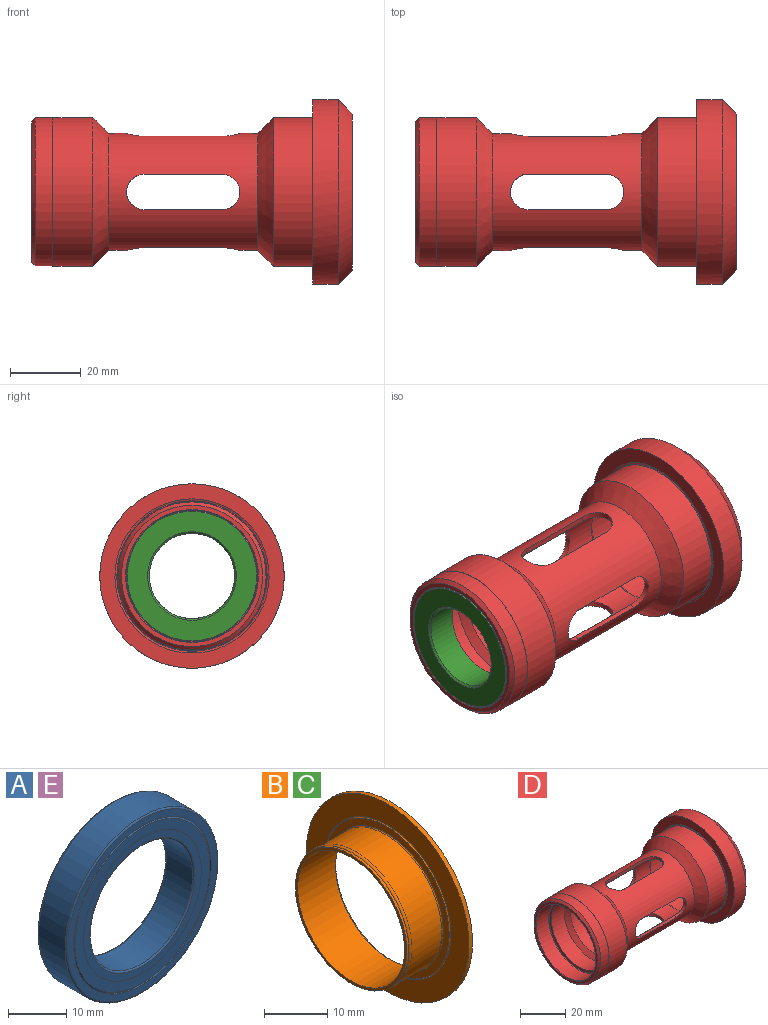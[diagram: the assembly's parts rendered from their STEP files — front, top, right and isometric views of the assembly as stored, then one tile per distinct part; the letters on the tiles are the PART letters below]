
ASSEMBLY  parts=5 mates=2
PART A: 38 faces, bbox 40x7x40 mm
  f0: torus R=15.5mm, axis (0,1,0), area 122.3mm2, adj f12,f37
  f1: cylinder r=12.5mm len=25mm, axis (0,1,0), area 502.7mm2, adj f2,f3
  f2: torus R=12.8mm, axis (0,1,0), area 37.3mm2, adj f1,f4
  f3: torus R=12.8mm, axis (0,1,0), area 37.3mm2, adj f1,f5
  f4: plane 28.62x28.62mm, normal (0,-1,0), area 128.4mm2, adj f2,f6
  f5: plane 28.62x28.62mm, normal (0,1,0), area 128.4mm2, adj f3,f8
  f6: cylinder r=14.31mm len=28.62mm, axis (0,1,0), area 62.9mm2, adj f4,f9
  f7: torus R=15.5mm, axis (0,1,0), area 122.3mm2, adj f10,f36
  f8: cylinder r=14.31mm len=28.62mm, axis (0,1,0), area 62.9mm2, adj f5,f11
  f9: plane 29.2x29.2mm, normal (0,-1,0), area 26.5mm2, adj f6,f10
  f10: cylinder r=14.6mm len=29.2mm, axis (0,1,0), area 113.9mm2, adj f7,f9
  f11: plane 29.2x29.2mm, normal (0,1,0), area 26.5mm2, adj f8,f12
  f12: cylinder r=14.6mm len=29.2mm, axis (0,1,0), area 113.9mm2, adj f0,f11
  f13: torus R=15.5mm, axis (0,1,0), area 146.2mm2, adj f35,f37
  f14: cylinder r=18.5mm len=37mm, axis (0,1,0), area 743.9mm2, adj f15,f16
  f15: torus R=18.2mm, axis (0,1,0), area 54.5mm2, adj f14,f17
  f16: torus R=18.2mm, axis (0,1,0), area 54.5mm2, adj f14,f18
  f17: plane 36.4x36.4mm, normal (0,-1,0), area 161.5mm2, adj f15,f19
  f18: plane 36.4x36.4mm, normal (0,1,0), area 161.5mm2, adj f16,f20
  f19: cylinder r=16.73mm len=33.46mm, axis (0,1,0), area 35.7mm2, adj f17,f21
  f20: cylinder r=16.73mm len=33.46mm, axis (0,1,0), area 35.7mm2, adj f18,f22
  f21: cone r=16.56mm half-angle=45deg, axis (0,1,0), area 50mm2, adj f19,f23
  f22: cone r=16.56mm half-angle=45deg, axis (0,-1,0), area 50mm2, adj f20,f24
  f23: plane 32.78x32.78mm, normal (0,-1,0), area 199.7mm2, adj f21,f25
  f24: plane 32.78x32.78mm, normal (0,1,0), area 199.7mm2, adj f22,f26
  f25: cylinder r=14.32mm len=28.64mm, axis (0,-1,0), area 62.1mm2, adj f23,f27
  f26: cylinder r=14.32mm len=28.64mm, axis (0,1,0), area 62.1mm2, adj f24,f28
  f27: plane 33.46x33.46mm, normal (0,1,0), area 235.1mm2, adj f25,f29
  f28: plane 33.46x33.46mm, normal (0,-1,0), area 235.1mm2, adj f26,f31
  f29: cylinder r=16.73mm len=33.46mm, axis (0,1,0), area 1.1mm2, adj f27,f32
  f30: torus R=15.5mm, axis (0,1,0), area 146.2mm2, adj f33,f36
  f31: cylinder r=16.73mm len=33.46mm, axis (0,1,0), area 1.1mm2, adj f28,f34
  f32: plane 33.46x33.46mm, normal (0,-1,0), area 34.1mm2, adj f29,f33
  f33: cylinder r=16.4mm len=32.8mm, axis (0,1,0), area 127.9mm2, adj f30,f32
  f34: plane 33.46x33.46mm, normal (0,1,0), area 34.1mm2, adj f31,f35
  f35: cylinder r=16.4mm len=32.8mm, axis (0,1,0), area 127.9mm2, adj f13,f34
  f36: plane 34.46x34.46mm, normal (0,-1,0), area 336.8mm2, adj f7,f30
  f37: plane 34.46x34.46mm, normal (0,1,0), area 336.8mm2, adj f0,f13
PART B: 12 faces, bbox 9x36.5x36.5 mm
  f0: cylinder r=12.5mm len=25mm, axis (-1,0,0), area 526.2mm2, adj f1,f11
  f1: torus R=12.25mm, axis (-1,0,0), area 56.7mm2, adj f0,f2
  f2: cylinder r=12.5mm len=25mm, axis (-1,0,0), area 37.3mm2, adj f1,f3
  f3: plane 25x25mm, normal (-1,0,0), area 38.5mm2, adj f2,f4
  f4: cylinder r=12mm len=24mm, axis (-1,0,0), area 640.9mm2, adj f3,f9
  f5: plane 36.5x36.5mm, normal (1,0,0), area 555.5mm2, adj f6,f9
  f6: cylinder r=18.25mm len=36.5mm, axis (-1,0,0), area 91.7mm2, adj f5,f7
  f7: plane 36.5x36.5mm, normal (-1,0,0), area 412.9mm2, adj f6,f10
  f8: plane 28x28mm, normal (-1,0,0), area 109mm2, adj f10,f11
  f9: cone r=12.5mm half-angle=45deg, axis (1,0,0), area 54.4mm2, adj f4,f5
  f10: torus R=14.2mm, axis (1,0,0), area 27.8mm2, adj f7,f8
  f11: torus R=12.7mm, axis (1,0,0), area 24.8mm2, adj f0,f8
PART C: same geometry as B
PART D: 44 faces, bbox 90.5x52x52 mm
  f0: plane 22x1.58mm, normal (0,-1,0), area 34.8mm2, adj f1,f3,f21,f31
  f1: cylinder r=5mm len=10mm, axis (0,0,1), area 24.2mm2, adj f0,f2,f21,f31
  f2: plane 22x1.58mm, normal (0,1,0), area 34.8mm2, adj f1,f3,f21,f31
  f3: cylinder r=5mm len=10mm, axis (0,0,1), area 24.2mm2, adj f0,f2,f21,f31
  f4: plane 22x1.58mm, normal (0,0,1), area 34.8mm2, adj f5,f7,f21,f31
  f5: cylinder r=5mm len=10mm, axis (0,1,0), area 24.2mm2, adj f4,f6,f21,f31
  f6: plane 22x1.58mm, normal (0,0,-1), area 34.8mm2, adj f5,f7,f21,f31
  f7: cylinder r=5mm len=10mm, axis (0,1,0), area 24.2mm2, adj f4,f6,f21,f31
  f8: plane 22x1.58mm, normal (0,1,0), area 34.8mm2, adj f9,f11,f21,f31
  f9: cylinder r=5mm len=10mm, axis (0,0,-1), area 24.2mm2, adj f8,f10,f21,f31
  f10: plane 22x1.58mm, normal (0,-1,0), area 34.8mm2, adj f9,f11,f21,f31
  f11: cylinder r=5mm len=10mm, axis (0,0,-1), area 24.2mm2, adj f8,f10,f21,f31
  f12: cylinder r=17mm len=34mm, axis (-1,0,0), area 1388.6mm2, adj f13,f32
  f13: plane 36.5x36.5mm, normal (1,0,0), area 138.4mm2, adj f12,f40
  f14: cylinder r=18.5mm len=37mm, axis (-1,0,0), area 877.6mm2, adj f40,f43
  f15: plane 44x44mm, normal (1,0,0), area 421.9mm2, adj f33,f43
  f16: cylinder r=26mm len=52mm, axis (-1,0,0), area 1184.4mm2, adj f17,f33
  f17: plane 52x52mm, normal (-1,0,0), area 637.6mm2, adj f16,f18
  f18: cone r=21.2mm half-angle=70deg, axis (-1,0,0), area 78.9mm2, adj f17,f39
  f19: cylinder r=21mm len=42mm, axis (-1,0,0), area 1451.4mm2, adj f20,f39
  f20: cone r=16.5mm half-angle=45deg, axis (1,0,0), area 749.7mm2, adj f19,f21
  f21: cylinder r=16.5mm len=42mm, axis (-1,0,0), area 3142.3mm2, adj f0,f1,f2,f3,f4,f5,f6,f7
  f22: cone r=21mm half-angle=45deg, axis (-1,0,0), area 749.7mm2, adj f21,f23
  f23: cylinder r=21mm len=42mm, axis (-1,0,0), area 1484.4mm2, adj f22,f24
  f24: plane 42x42mm, normal (-1,0,0), area 13.2mm2, adj f23,f25
  f25: cylinder r=20.9mm len=41.8mm, axis (-1,0,0), area 656.6mm2, adj f24,f34
  f26: plane 39.8x39.8mm, normal (-1,0,0), area 145.5mm2, adj f34,f42
  f27: cylinder r=18.5mm len=37mm, axis (-1,0,0), area 877.6mm2, adj f41,f42
  f28: plane 36.5x36.5mm, normal (-1,0,0), area 138.4mm2, adj f29,f41
  f29: cylinder r=17mm len=34mm, axis (-1,0,0), area 854.5mm2, adj f28,f30
  f30: cone r=15mm half-angle=45deg, axis (-1,0,0), area 284.3mm2, adj f29,f31
  f31: cylinder r=15mm len=49.5mm, axis (-1,0,0), area 3449.4mm2, adj f0,f1,f2,f3,f4,f5,f6,f7
  f32: cone r=17mm half-angle=45deg, axis (1,0,0), area 284.3mm2, adj f12,f31
  f33: cone r=26mm half-angle=45deg, axis (-1,0,0), area 853mm2, adj f15,f16
  f34: cone r=19.9mm half-angle=45deg, axis (1,0,0), area 181.3mm2, adj f25,f26
  f35: plane 22x1.58mm, normal (0,0,-1), area 34.8mm2, adj f21,f31,f36,f38
  f36: cylinder r=5mm len=10mm, axis (0,-1,0), area 24.2mm2, adj f21,f31,f35,f37
  f37: plane 22x1.58mm, normal (0,0,1), area 34.8mm2, adj f21,f31,f36,f38
  f38: cylinder r=5mm len=10mm, axis (0,-1,0), area 24.2mm2, adj f21,f31,f35,f37
  f39: torus R=21.2mm, axis (-1,0,0), area 41.6mm2, adj f18,f19
  f40: torus R=18.25mm, axis (1,0,0), area 45.4mm2, adj f13,f14
  f41: torus R=18.25mm, axis (-1,0,0), area 45.4mm2, adj f27,f28
  f42: cone r=18.5mm half-angle=45deg, axis (-1,0,0), area 33.1mm2, adj f26,f27
  f43: cone r=18.7mm half-angle=45deg, axis (1,0,0), area 33.1mm2, adj f14,f15
PART E: same geometry as A
PLACE A rot(axis=(0,0,-1),90deg) t=(44.25,0,0)mm
PLACE B t=(-0.5,0,0)mm
PLACE C rot(axis=(0,1,0),180deg) t=(0.5,0,0)mm
PLACE D at identity
PLACE E rot(axis=(0.71,-0.71,0),180deg) t=(-44.25,0,0)mm
MATE fastened A.f26 <-> D.f12  axis (-1,0,0) through (37.25,0,0)mm
MATE fastened E.f26 <-> D.f12  axis (1,0,0) through (-37.25,0,0)mm
